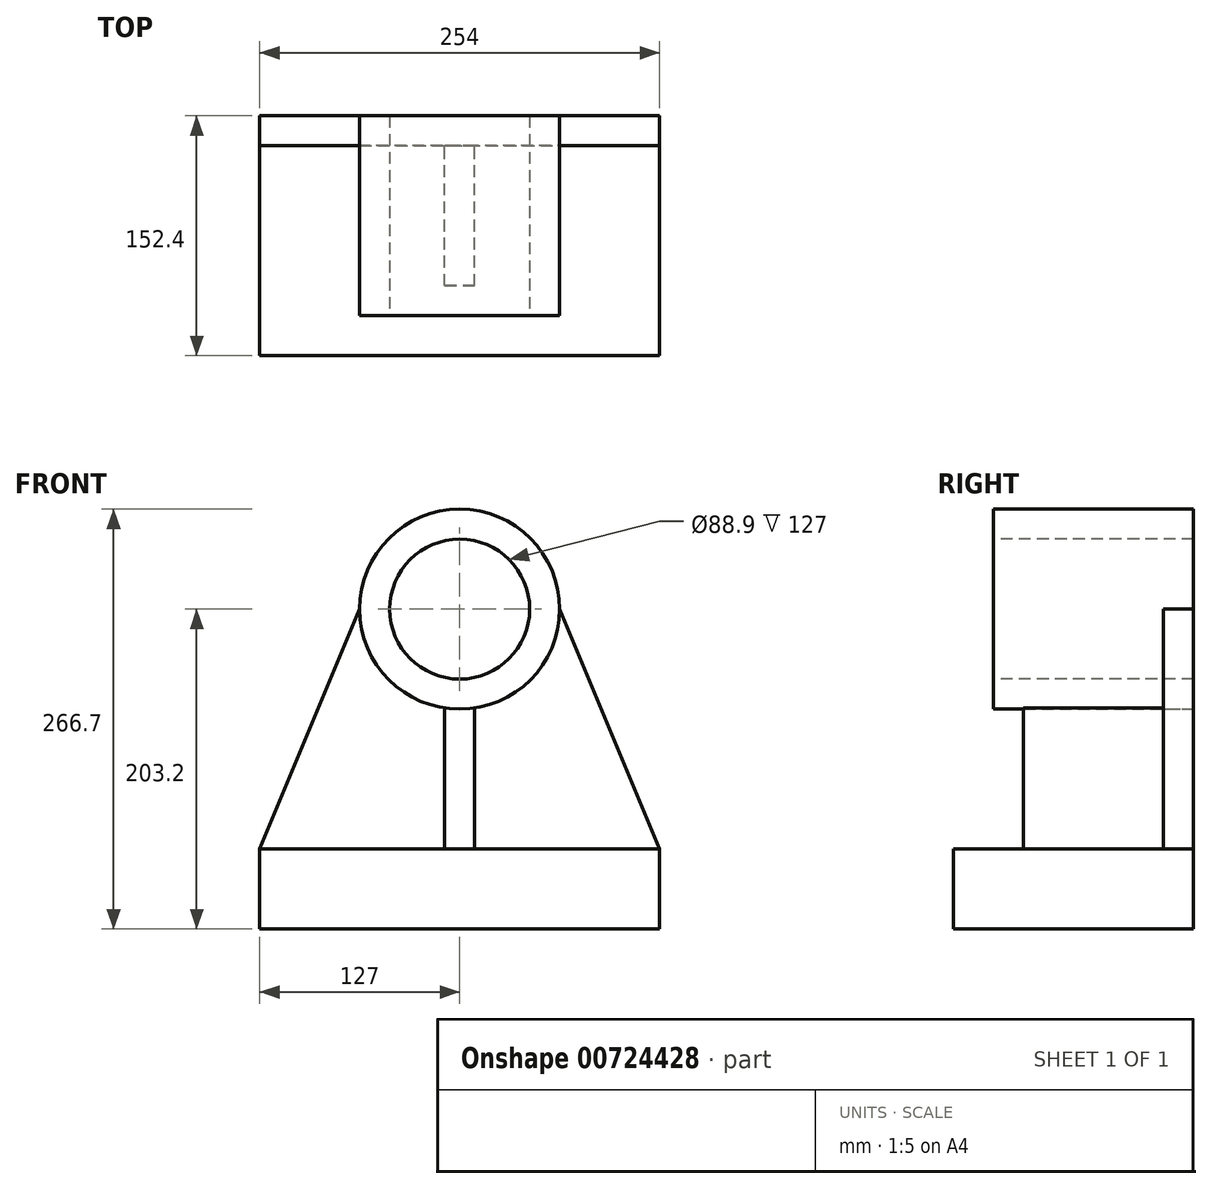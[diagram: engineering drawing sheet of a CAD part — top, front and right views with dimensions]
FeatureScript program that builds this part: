
annotation { "Feature Type Name" : "Feature", "Feature Type Description" : "" }
export const myFeature = defineFeature(function(context is Context, id is Id, definition is map)
    precondition{}
    {
        {
            var Q0;
            Q0=qCreatedBy(makeId("Front.planeOp"),FACE);
            var sketch = newSketch(context, id + "F0", { "sketchPlane" : qUnion([Q0])});
            skLineSegment(sketch, "E0.bottom", {"start": v(127, -25.4) * mm, "end": v(-127, -25.4) * mm});
            skLineSegment(sketch, "E0.top", {"start": v(127, 25.4) * mm, "end": v(-127, 25.4) * mm});
            skLineSegment(sketch, "E0.left", {"start": v(127, -25.4) * mm, "end": v(127, 25.4) * mm});
            skLineSegment(sketch, "E0.right", {"start": v(-127, -25.4) * mm, "end": v(-127, 25.4) * mm});
            skPoint(sketch, "E0.middle", {"position": v(0, 0) * mm});
            skLineSegment(sketch, "E1", {"start": v(0, 0) * mm, "end": v(0, 177.8) * mm, "construction": true});
            skCircle(sketch, "E2", {"center": v(0, 177.8) * mm, "radius": 63.5 * mm});
            skLineSegment(sketch, "E3", {"start": v(-127, 25.4) * mm, "end": v(-63.5, 177.8) * mm});
            skLineSegment(sketch, "E4", {"start": v(127, 25.4) * mm, "end": v(63.5, 177.8) * mm});
            skLineSegment(sketch, "E5", {"start": v(-63.5, 177.8) * mm, "end": v(63.5, 177.8) * mm, "construction": true});
            skSolve(sketch);
        }
        {
            var Q0;
            Q0=makeQuery(id+"F0.imprint","IMPRINT",FACE,{"disambiguationData":[TD([[makeQuery(id+"F0.imprint","IMPRINT",EDGE,{"derivedFrom":sQuery(id+"F0.wireOp",EDGE,"E0.bottom")}),-1.0]])]});
            extrude(context, id + "F1", {"entities" : qUnion([Q0]), "depth" : 152.4 * mm, "offsetDistance" : 25.4 * mm});
        }
        {
            var Q0;
            {var subQ0=sQuery(id+"F0.wireOp",EDGE,"E2");var subQ1=makeQuery(id+"F0.imprint","INTERSECT",VERTEX,{"derivedFrom":[subQ0,sQuery(id+"F0.wireOp",EDGE,"E3")]});Q0=makeQuery(id+"F0.imprint","IMPRINT",FACE,{"disambiguationData":[TD([[makeQuery(id+"F0.imprint","IMPRINT",EDGE,{"disambiguationData":[TD([[subQ1,1.0]])],"derivedFrom":subQ0}),1.0]])]});}
            var Q1;
            Q1=sQuery(id+"F0.wireOp",EDGE,"E2");
            extrude(context, id + "F2", {"entities" : qUnion([Q0]), "surfaceEntities" : qUnion([Q1]), "depth" : 127 * mm, "offsetDistance" : 25.4 * mm});
        }
        {
            var Q0;
            Q0=makeQuery(id+"F0.imprint","IMPRINT",FACE,{"disambiguationData":[TD([[makeQuery(id+"F0.imprint","IMPRINT",EDGE,{"derivedFrom":sQuery(id+"F0.wireOp",EDGE,"E0.top")}),-1.0]])]});
            extrude(context, id + "F3", {"entities" : qUnion([Q0]), "depth" : 19.05 * mm, "offsetDistance" : 25.4 * mm});
        }
        {
            var Q0;
            Q0=makeQuery(id+"F2.opExtrude","CAP_FACE",FACE,{"disambiguationData":[OSD([sQuery(id+"F0.wireOp",EDGE,"E2")])],"isStart":false});
            var sketch = newSketch(context, id + "F4", { "sketchPlane" : qUnion([Q0])});
            skLineSegment(sketch, "E6", {"start": v(0, 241.3) * mm, "end": v(0, 114.3) * mm, "construction": true});
            skCircle(sketch, "E7.0", {"center": v(0, 177.8) * mm, "radius": 44.45 * mm});
            skSolve(sketch);
        }
        {
            var Q0;
            Q0=makeQuery(id+"F4.imprint","IMPRINT",FACE,{"disambiguationData":[TD([[makeQuery(id+"F4.imprint","IMPRINT",EDGE,{"derivedFrom":sQuery(id+"F4.wireOp",EDGE,"E7.0")}),1.0]])]});
            var Q1;
            Q1=sQuery(id+"F4.wireOp",EDGE,"E7.0");
            extrude(context, id + "F5", {"entities" : qUnion([Q0]), "operationType" : NewBodyOperationType.REMOVE, "surfaceEntities" : qUnion([Q1]), "endBound" : BoundingType.THROUGH_ALL, "oppositeDirection" : true, "depth" : 25.4 * mm, "offsetDistance" : 25.4 * mm});
        }
        {
            var Q0;
            Q0=makeQuery(id+"F3.opExtrude","CAP_FACE",FACE,{"disambiguationData":[OSD([sQuery(id+"F0.wireOp",EDGE,"E0.top"),sQuery(id+"F0.wireOp",EDGE,"E2"),sQuery(id+"F0.wireOp",EDGE,"E3"),sQuery(id+"F0.wireOp",EDGE,"E4")])],"isStart":false});
            var sketch = newSketch(context, id + "F6", { "sketchPlane" : qUnion([Q0])});
            skLineSegment(sketch, "E8", {"start": v(0, 114.3) * mm, "end": v(0, 25.4) * mm, "construction": true});
            skLineSegment(sketch, "E9.0", {"start": v(-9.53, 115.02) * mm, "end": v(-9.52, 25.4) * mm});
            skLineSegment(sketch, "E10.0", {"start": v(9.52, 115.02) * mm, "end": v(9.53, 25.4) * mm});
            skLineSegment(sketch, "E11", {"start": v(-9.52, 25.4) * mm, "end": v(9.53, 25.4) * mm});
            skSolve(sketch);
        }
        {
            var Q0;
            {var subQ0=sQuery(id+"F6.wireOp",EDGE,"E9.0");Q0=makeQuery(id+"F6.imprint","IMPRINT",FACE,{"disambiguationData":[TD([[makeQuery(id+"F6.imprint","IMPRINT",EDGE,{"derivedFrom":subQ0}),1.0]])]});}
            extrude(context, id + "F7", {"entities" : qUnion([Q0]), "depth" : 88.9 * mm, "offsetDistance" : 25.4 * mm});
        }
    });
